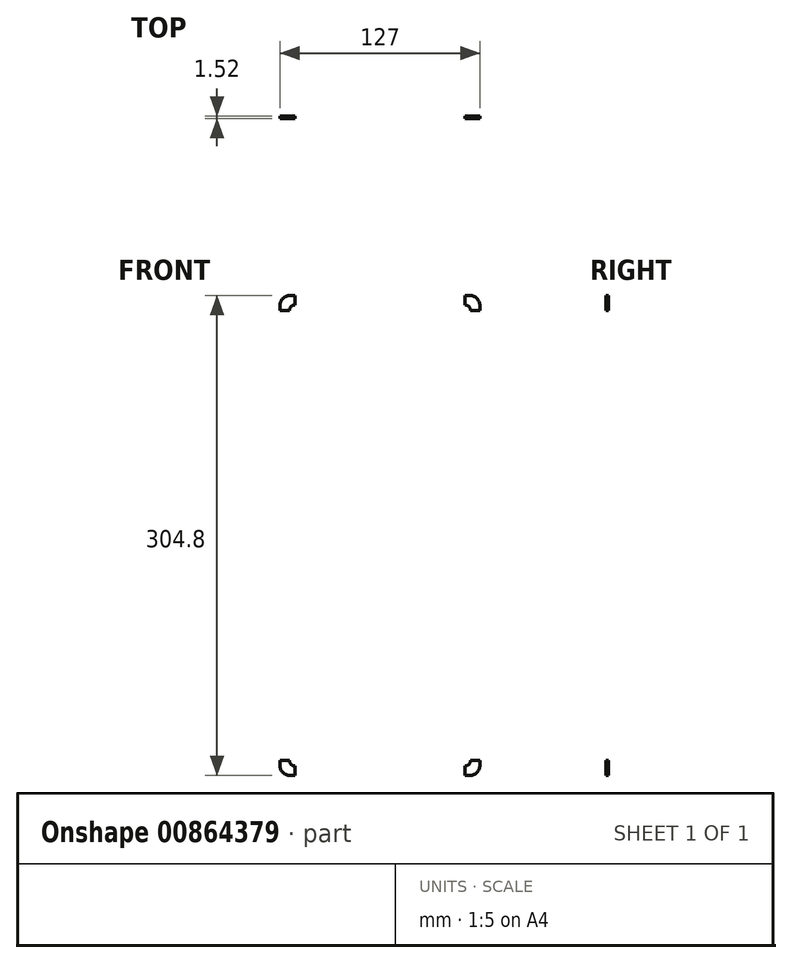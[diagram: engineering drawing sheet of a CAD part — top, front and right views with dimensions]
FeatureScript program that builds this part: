
annotation { "Feature Type Name" : "Feature", "Feature Type Description" : "" }
export const myFeature = defineFeature(function(context is Context, id is Id, definition is map)
    precondition{}
    {
        {
            var Q0;
            Q0=qCreatedBy(makeId("Front.planeOp"),FACE);
            var sketch = newSketch(context, id + "F0", { "sketchPlane" : qUnion([Q0])});
            skLineSegment(sketch, "E0.bottom", {"start": v(-100.35, 262.84) * mm, "end": v(13.95, 262.84) * mm});
            skLineSegment(sketch, "E0.top", {"start": v(-100.35, -41.96) * mm, "end": v(13.95, -41.96) * mm});
            skLineSegment(sketch, "E0.left", {"start": v(-106.7, 256.49) * mm, "end": v(-106.7, -35.61) * mm});
            skLineSegment(sketch, "E0.right", {"start": v(20.3, 256.49) * mm, "end": v(20.3, -35.61) * mm});
            skPoint(sketch, "E1.visualSharp", {"position": v(-106.7, 262.84) * mm});
            skArc(sketch, "E1.filletArc", {"start": v(-100.35, 262.84) * mm, "mid": v(-104.84, 260.98) * mm, "end": v(-106.7, 256.49) * mm});
            skPoint(sketch, "E2.visualSharp", {"position": v(20.3, 262.84) * mm});
            skArc(sketch, "E2.filletArc", {"start": v(20.3, 256.49) * mm, "mid": v(18.44, 260.98) * mm, "end": v(13.95, 262.84) * mm});
            skPoint(sketch, "E3.visualSharp", {"position": v(-106.7, -41.96) * mm});
            skArc(sketch, "E3.filletArc", {"start": v(-106.7, -35.61) * mm, "mid": v(-104.84, -40.1) * mm, "end": v(-100.35, -41.96) * mm});
            skPoint(sketch, "E4.visualSharp", {"position": v(20.3, -41.96) * mm});
            skArc(sketch, "E4.filletArc", {"start": v(13.95, -41.96) * mm, "mid": v(18.44, -40.1) * mm, "end": v(20.3, -35.61) * mm});
            skLineSegment(sketch, "E5.bottom", {"start": v(-106.7, 262.84) * mm, "end": v(-97.17, 262.84) * mm});
            skLineSegment(sketch, "E5.top", {"start": v(-106.7, 253.31) * mm, "end": v(-97.17, 253.31) * mm});
            skLineSegment(sketch, "E5.left", {"start": v(-106.7, 262.84) * mm, "end": v(-106.7, 253.31) * mm});
            skLineSegment(sketch, "E5.right", {"start": v(-97.17, 262.84) * mm, "end": v(-97.17, 253.31) * mm});
            skCircle(sketch, "E6", {"center": v(-97.17, 253.31) * mm, "radius": 3.57 * mm});
            skLineSegment(sketch, "E7.bottom", {"start": v(20.3, 262.84) * mm, "end": v(10.78, 262.84) * mm});
            skLineSegment(sketch, "E7.top", {"start": v(20.3, 253.31) * mm, "end": v(10.78, 253.31) * mm});
            skLineSegment(sketch, "E7.left", {"start": v(20.3, 262.84) * mm, "end": v(20.3, 253.31) * mm});
            skLineSegment(sketch, "E7.right", {"start": v(10.78, 262.84) * mm, "end": v(10.78, 253.31) * mm});
            skCircle(sketch, "E8", {"center": v(10.78, 253.31) * mm, "radius": 3.57 * mm});
            skLineSegment(sketch, "E9.bottom", {"start": v(-106.7, -41.96) * mm, "end": v(-97.17, -41.96) * mm});
            skLineSegment(sketch, "E9.top", {"start": v(-106.7, -32.44) * mm, "end": v(-97.17, -32.44) * mm});
            skLineSegment(sketch, "E9.left", {"start": v(-106.7, -41.96) * mm, "end": v(-106.7, -32.44) * mm});
            skLineSegment(sketch, "E9.right", {"start": v(-97.17, -41.96) * mm, "end": v(-97.17, -32.44) * mm});
            skLineSegment(sketch, "E10.bottom", {"start": v(20.3, -41.96) * mm, "end": v(10.78, -41.96) * mm});
            skLineSegment(sketch, "E10.top", {"start": v(20.3, -32.44) * mm, "end": v(10.78, -32.44) * mm});
            skLineSegment(sketch, "E10.left", {"start": v(20.3, -41.96) * mm, "end": v(20.3, -32.44) * mm});
            skLineSegment(sketch, "E10.right", {"start": v(10.78, -41.96) * mm, "end": v(10.78, -32.44) * mm});
            skCircle(sketch, "E11", {"center": v(-97.17, -32.44) * mm, "radius": 3.57 * mm});
            skCircle(sketch, "E12", {"center": v(10.78, -32.44) * mm, "radius": 3.57 * mm});
            skSolve(sketch);
        }
        {
            var Q0;
            {var subQ3=sQuery(id+"F0.wireOp",EDGE,"E1.filletArc");Q0=makeQuery(id+"F0.imprint","IMPRINT",FACE,{"disambiguationData":[TD([[makeQuery(id+"F0.imprint","IMPRINT",EDGE,{"derivedFrom":subQ3}),1.0]])]});}
            var Q1;
            {var subQ12=sQuery(id+"F0.wireOp",EDGE,"E0.bottom");Q1=makeQuery(id+"F0.imprint","IMPRINT",FACE,{"disambiguationData":[TD([[makeQuery(id+"F0.imprint","IMPRINT",EDGE,{"derivedFrom":subQ12}),-1.0]])]});}
            var Q2;
            {var subQ3=sQuery(id+"F0.wireOp",EDGE,"E2.filletArc");Q2=makeQuery(id+"F0.imprint","IMPRINT",FACE,{"disambiguationData":[TD([[makeQuery(id+"F0.imprint","IMPRINT",EDGE,{"derivedFrom":subQ3}),1.0]])]});}
            var Q3;
            {var subQ3=sQuery(id+"F0.wireOp",EDGE,"E3.filletArc");Q3=makeQuery(id+"F0.imprint","IMPRINT",FACE,{"disambiguationData":[TD([[makeQuery(id+"F0.imprint","IMPRINT",EDGE,{"derivedFrom":subQ3}),1.0]])]});}
            var Q4;
            {var subQ3=sQuery(id+"F0.wireOp",EDGE,"E4.filletArc");Q4=makeQuery(id+"F0.imprint","IMPRINT",FACE,{"disambiguationData":[TD([[makeQuery(id+"F0.imprint","IMPRINT",EDGE,{"derivedFrom":subQ3}),1.0]])]});}
            extrude(context, id + "F1", {"entities" : qUnion([Q0, Q1, Q2, Q3, Q4]), "depth" : 1.52 * mm, "offsetDistance" : 25.4 * mm});
        }
    });
